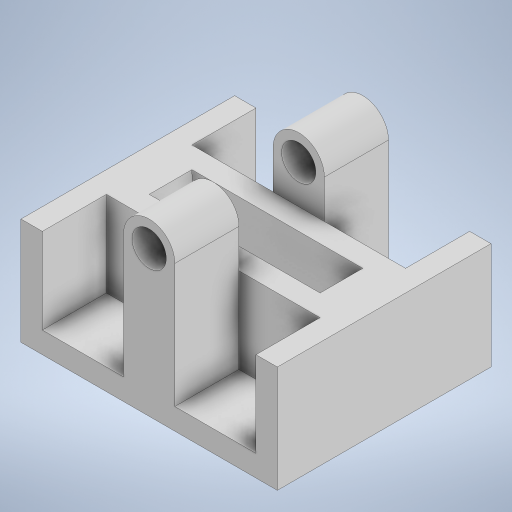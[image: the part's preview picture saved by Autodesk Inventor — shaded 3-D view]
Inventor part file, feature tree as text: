
AUTODESK INVENTOR PART (.ipt)
format: ipt  version: 2024 (Build 280153000, 153)  size: 286,720 bytes
history: native  units: mm
features: sketch x4, extrude x3, revolve x1, plane x1, mirror x1
ambient origin geometry x8: Origin, YZ Plane, XZ Plane, XY Plane, X Axis, Y Axis, Z Axis, Center Point
bodies: Solid1 (feature_tree)
feature tree (10):
  extrude  "Extrusion1"  Depth=25.0mm
  extrude  "Extrusion2"  Depth=12.0mm
  extrude  "Extrusion3"  Depth=25.0mm TaperAngle=0.0deg
  revolve  "Revolution1"  [1 undecoded]
  plane  "Work Plane1"
  mirror  "Mirror1"
  sketch  "Sketch2"  dims[d0=60.0mm d9=25.0mm]
  sketch  "Sketch3"  dims[d12=8.0mm d13=12.0mm]
  sketch  "Sketch4"  dims[d14=9.0mm d15=25.0mm d16=0.0mm]
  sketch  "Sketch5"  dims[d17=5.0mm d18=5.0mm d19=5.0mm d20=5.0mm d21=15.0mm d22=0.0mm d23=15.0mm d25=10.0mm d26=0.0mm d27=20.0mm d28=5.0mm d29=90.0deg d30=25.0mm]
note: 1 required parameter value undecoded (feature->parameter linkage not recoverable at this tier; creation-order binding heuristic only, values carry confidence <= 0.55)
